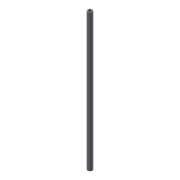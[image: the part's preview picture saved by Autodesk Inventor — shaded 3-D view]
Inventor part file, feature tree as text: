
AUTODESK INVENTOR PART (.ipt)
format: ipt  version: 2017 (Build 210142000, 142)  size: 69,632 bytes
history: native  units: in
note: dims shown in document units (in); Inventor stores cm internally (conversion verified against a paired STEP export)
features: extrude x1, sketch x1
ambient origin geometry x8: Origin, YZ Plane, XZ Plane, XY Plane, X Axis, Y Axis, Z Axis, Center Point
bodies: Solid1 (feature_tree)
feature tree (2):
  extrude  "Extrusion1"  Depth=0.3937in
  sketch  "Sketch1"  dims[d0=0.2756in d1=0.3937in d2=11.5625in d3=0.0in]
